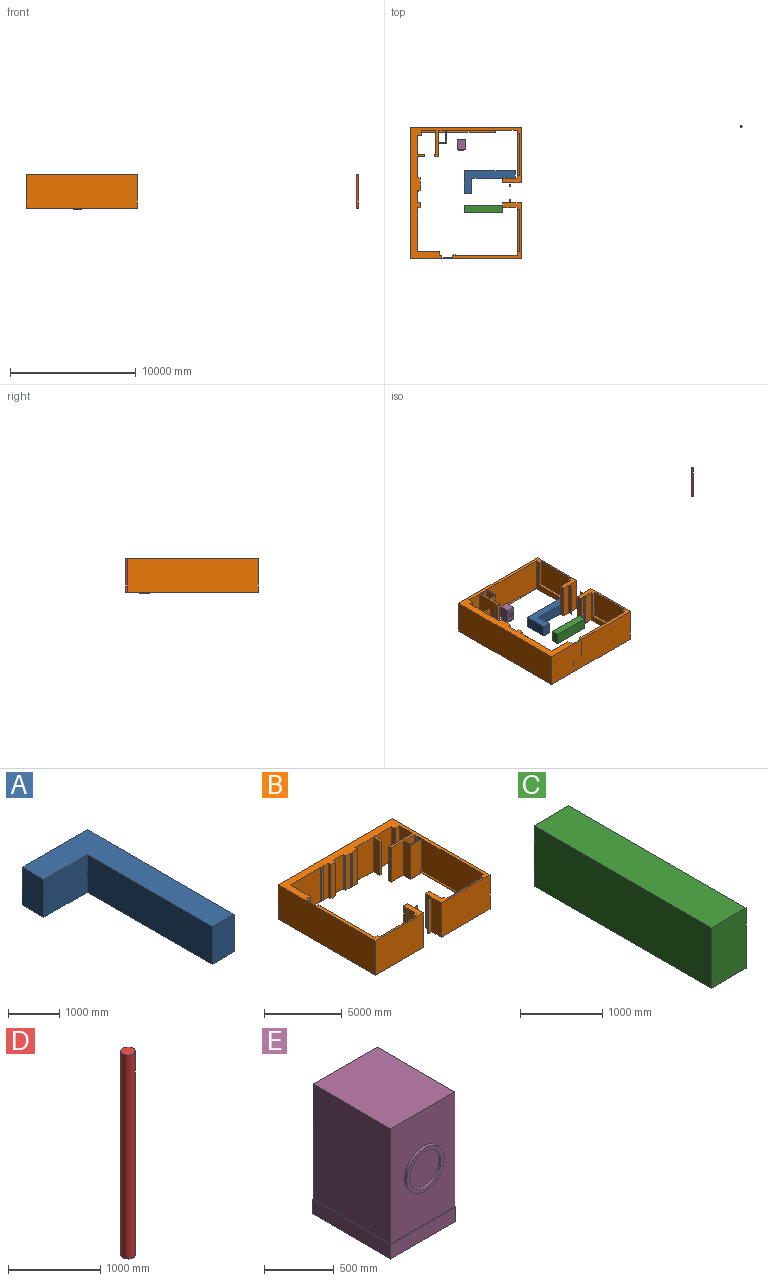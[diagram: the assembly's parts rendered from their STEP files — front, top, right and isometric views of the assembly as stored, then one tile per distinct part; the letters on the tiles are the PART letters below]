
ASSEMBLY  parts=5 mates=9
PART A: 8 faces, bbox 1800x4050x900 mm
  f0: plane 900x600mm, normal (-1,0,0), area 540000mm2, adj f1,f5,f6,f7
  f1: plane 1200x900mm, normal (0,-1,0), area 1080000mm2, adj f0,f2,f6,f7
  f2: plane 3450x900mm, normal (-1,0,0), area 3105000mm2, adj f1,f3,f6,f7
  f3: plane 900x600mm, normal (0,-1,0), area 540000mm2, adj f2,f4,f6,f7
  f4: plane 4050x900mm, normal (1,0,0), area 3645000mm2, adj f3,f5,f6,f7
  f5: plane 1800x900mm, normal (0,1,0), area 1620000mm2, adj f0,f4,f6,f7
  f6: plane 4050x1800mm, normal (0,0,-1), area 3150000mm2, adj f0,f1,f2,f3,f4,f5
  f7: plane 4050x1800mm, normal (0,0,1), area 3150000mm2, adj f0,f1,f2,f3,f4,f5
PART B: 107 faces, bbox 10433x8851.6x2700 mm
  f0: plane 2234.92x220mm, normal (-1,0,0), area 491681.4mm2, adj f40,f42,f94,f106
  f1: plane 2234.92x220mm, normal (-1,0,0), area 491681.4mm2, adj f6,f8,f94,f105
  f2: plane 2700x1080mm, normal (0,-1,0), area 2916000mm2, adj f3,f93,f94,f95
  f3: plane 2700x675mm, normal (-1,0,0), area 1822500mm2, adj f2,f4,f94,f95
  f4: plane 2700x1020mm, normal (0,-1,0), area 2744496.7mm2, adj f3,f5,f94,f95,f103
  f5: plane 5595x2700mm, normal (-1,0,0), area 15106500mm2, adj f4,f8,f94,f95
  f6: plane 3335x2234.92mm, normal (0,1,0), area 7453443.4mm2, adj f1,f7,f94,f105
  f7: plane 2234.92x220mm, normal (1,0,0), area 491681.4mm2, adj f6,f8,f94,f105
  f8: plane 3805x2700mm, normal (0,1,0), area 2820056.6mm2, adj f1,f5,f7,f9,f94,f95,f105
  f9: plane 2700x595mm, normal (1,0,0), area 1606500mm2, adj f8,f10,f94,f95
  f10: plane 2700x40mm, normal (0,-1,0), area 108000mm2, adj f9,f11,f94,f95
  f11: plane 2700x150mm, normal (1,0,0), area 405000mm2, adj f10,f12,f94,f95
  f12: plane 2700x40mm, normal (0,1,0), area 108000mm2, adj f11,f13,f94,f95
  f13: plane 2700x165.28mm, normal (1,0,0), area 446266.3mm2, adj f12,f14,f94,f95
  f14: plane 2700x40.98mm, normal (0,-1,0), area 110641.5mm2, adj f13,f15,f94,f95
  f15: plane 2700x143.9mm, normal (1,0,0), area 388534.6mm2, adj f14,f16,f94,f95
  f16: plane 2700x40.98mm, normal (0,1,0), area 110641.5mm2, adj f15,f17,f94,f95
  f17: plane 2700x75.81mm, normal (1,0,0), area 204699.1mm2, adj f16,f18,f94,f95
  f18: plane 2700x370mm, normal (0,1,0), area 999000mm2, adj f17,f19,f94,f95
  f19: plane 2700x560mm, normal (-1,0,0), area 1512000mm2, adj f18,f20,f94,f95
  f20: plane 2700x310.51mm, normal (0,1,0), area 838376.4mm2, adj f19,f21,f94,f95
  f21: plane 2700x50mm, normal (-1,0,0), area 135000mm2, adj f20,f22,f94,f95
  f22: plane 2700x310.51mm, normal (0,-1,0), area 838376.4mm2, adj f21,f23,f94,f95
  f23: plane 2700x870mm, normal (-1,0,0), area 2349000mm2, adj f22,f24,f94,f95
  f24: plane 4429x2700mm, normal (0,-1,0), area 11958300mm2, adj f23,f25,f94,f95
  f25: plane 8851.56x2700mm, normal (1,0,0), area 23899202.3mm2, adj f24,f26,f94,f95
  f26: plane 10433x2700mm, normal (0,1,0), area 28169100mm2, adj f25,f27,f94,f95
  f27: plane 8851.56x2700mm, normal (-1,0,0), area 23899202.3mm2, adj f26,f28,f94,f95
  f28: plane 4424x2700mm, normal (0,-1,0), area 11944800mm2, adj f27,f29,f94,f95
  f29: plane 2700x870mm, normal (1,0,0), area 2349000mm2, adj f28,f30,f94,f95
  f30: plane 2700x264.49mm, normal (0,-1,0), area 714123.6mm2, adj f29,f31,f94,f95
  f31: plane 2700x50mm, normal (1,0,0), area 135000mm2, adj f30,f32,f94,f95
  f32: plane 2700x264.49mm, normal (0,1,0), area 714123.6mm2, adj f31,f33,f94,f95
  f33: plane 2700x560mm, normal (1,0,0), area 1512000mm2, adj f32,f34,f94,f95
  f34: plane 2700x370mm, normal (0,1,0), area 999000mm2, adj f33,f35,f94,f95
  f35: plane 2700x325mm, normal (-1,0,0), area 877500mm2, adj f34,f36,f94,f95
  f36: plane 2700x40mm, normal (0,1,0), area 108000mm2, adj f35,f37,f94,f95
  f37: plane 2700x150mm, normal (-1,0,0), area 405000mm2, adj f36,f38,f94,f95
  f38: plane 2700x40mm, normal (0,-1,0), area 108000mm2, adj f37,f39,f94,f95
  f39: plane 2700x655mm, normal (-1,0,0), area 1768500mm2, adj f38,f42,f94,f95
  f40: plane 3350x2234.92mm, normal (0,1,0), area 7486967.1mm2, adj f0,f41,f94,f106
  f41: plane 2234.92x220mm, normal (1,0,0), area 491681.4mm2, adj f40,f42,f94,f106
  f42: plane 3800x2700mm, normal (0,1,0), area 2773032.9mm2, adj f0,f39,f41,f43,f94,f95,f106
  f43: plane 4916.91x2700mm, normal (1,0,0), area 13275652.3mm2, adj f42,f44,f94,f95
  f44: plane 2700x40mm, normal (0,-1,0), area 108000mm2, adj f43,f45,f94,f95
  f45: plane 2700x150mm, normal (1,0,0), area 405000mm2, adj f44,f46,f94,f95
  f46: plane 2700x40mm, normal (0,1,0), area 108000mm2, adj f45,f47,f94,f95
  f47: plane 2700x23.09mm, normal (1,0,0), area 62347.7mm2, adj f46,f48,f94,f95
  f48: plane 2700x200mm, normal (0,1,0), area 540000mm2, adj f47,f49,f94,f95
  f49: plane 2700x870mm, normal (1,0,0), area 2349000mm2, adj f48,f50,f94,f95
  f50: plane 2700x200mm, normal (0,-1,0), area 540000mm2, adj f49,f51,f94,f95
  f51: plane 2700x170mm, normal (1,0,0), area 459000mm2, adj f50,f52,f94,f95
  f52: plane 2700x300mm, normal (0,-1,0), area 810000mm2, adj f51,f53,f94,f95
  f53: plane 2700x1800mm, normal (1,0,0), area 4860000mm2, adj f52,f54,f94,f95
  f54: plane 2785x2700mm, normal (0,-1,0), area 7519500mm2, adj f53,f55,f94,f95
  f55: plane 2700x40mm, normal (-1,0,0), area 108000mm2, adj f54,f56,f94,f95
  f56: plane 2700x150mm, normal (0,-1,0), area 405000mm2, adj f55,f57,f94,f95
  f57: plane 2700x40mm, normal (1,0,0), area 108000mm2, adj f56,f58,f94,f95
  f58: plane 2700x525mm, normal (0,-1,0), area 1417500mm2, adj f57,f59,f94,f95
  f59: plane 2700x230mm, normal (-1,0,0), area 621000mm2, adj f58,f60,f94,f95
  f60: plane 2700x445mm, normal (0,-1,0), area 1201500mm2, adj f59,f61,f94,f95
  f61: plane 2700x230mm, normal (1,0,0), area 621000mm2, adj f60,f62,f94,f95
  f62: plane 2700x900mm, normal (0,-1,0), area 2430000mm2, adj f61,f63,f94,f95
  f63: plane 2700x70.97mm, normal (-1,0,0), area 191611.9mm2, adj f62,f64,f94,f95
  f64: plane 2700x32.69mm, normal (0,1,0), area 88264.4mm2, adj f63,f65,f94,f95
  f65: plane 2700x66.16mm, normal (-1,0,0), area 178631.3mm2, adj f64,f66,f94,f95
  f66: plane 2700x32.69mm, normal (0,-1,0), area 88264.4mm2, adj f65,f67,f94,f95
  f67: plane 2700x92.87mm, normal (-1,0,0), area 250756.8mm2, adj f66,f68,f94,f95
  f68: plane 2700x445mm, normal (0,-1,0), area 1201500mm2, adj f67,f69,f94,f95
  f69: plane 2700x40mm, normal (-1,0,0), area 108000mm2, adj f68,f70,f94,f95
  f70: plane 2700x150mm, normal (0,-1,0), area 405000mm2, adj f69,f71,f94,f95
  f71: plane 2700x40mm, normal (1,0,0), area 108000mm2, adj f70,f72,f94,f95
  f72: plane 2700x465mm, normal (0,-1,0), area 1255500mm2, adj f71,f73,f94,f95
  f73: plane 2700x230mm, normal (1,0,0), area 621000mm2, adj f72,f74,f94,f95
  f74: plane 2700x1660mm, normal (0,-1,0), area 4469250mm2, adj f73,f75,f94,f95,f96,f97,f98,f99
  f75: plane 2700x610mm, normal (-1,0,0), area 1647000mm2, adj f74,f76,f94,f95
  f76: plane 2700x160mm, normal (0,-1,0), area 432000mm2, adj f75,f77,f94,f95
  f77: plane 2700x610mm, normal (1,0,0), area 1647000mm2, adj f76,f78,f94,f95
  f78: plane 2700x1530mm, normal (0,-1,0), area 4131000mm2, adj f77,f79,f94,f95
  f79: plane 2700x320mm, normal (-1,0,0), area 864000mm2, adj f78,f80,f94,f95
  f80: plane 2700x410mm, normal (0,-1,0), area 1097496.7mm2, adj f79,f81,f94,f95,f102
  f81: plane 2700x1155mm, normal (-1,0,0), area 3118500mm2, adj f80,f82,f94,f95
  f82: plane 2700x1940mm, normal (0,1,0), area 5228496.7mm2, adj f81,f83,f94,f95,f102
  f83: plane 2700x65mm, normal (1,0,0), area 175500mm2, adj f82,f84,f94,f95
  f84: plane 2700x160mm, normal (0,1,0), area 432000mm2, adj f83,f93,f94,f95
  f85: plane 2700x625mm, normal (1,0,0), area 1687500mm2, adj f86,f92,f94,f95
  f86: plane 2700x970mm, normal (0,-1,0), area 2609496.7mm2, adj f85,f87,f94,f95,f101
  f87: plane 2700x100mm, normal (-1,0,0), area 270000mm2, adj f86,f88,f94,f95
  f88: plane 2700x40mm, normal (0,1,0), area 108000mm2, adj f87,f89,f94,f95
  f89: plane 2700x150mm, normal (-1,0,0), area 405000mm2, adj f88,f90,f94,f95
  f90: plane 2700x40mm, normal (0,-1,0), area 108000mm2, adj f89,f91,f94,f95
  f91: plane 2700x375mm, normal (-1,0,0), area 1012500mm2, adj f90,f92,f94,f95
  f92: plane 2700x970mm, normal (0,1,0), area 2609496.7mm2, adj f85,f91,f94,f95,f101
  f93: plane 2700x250mm, normal (-1,0,0), area 675000mm2, adj f2,f84,f94,f95
  f94: plane 10433x8851.56mm, normal (0,0,1), area 13950447.5mm2, adj f0,f1,f2,f3,f4,f5,f6,f7
  f95: plane 10433x8851.56mm, normal (0,0,-1), area 15421147.5mm2, adj f2,f3,f4,f5,f8,f9,f10,f11
  f96: plane 150x40mm, normal (0,0,1), area 6000mm2, adj f74,f97,f99,f100
  f97: plane 85x40mm, normal (-1,0,0), area 3400mm2, adj f74,f96,f98,f100
  f98: plane 150x40mm, normal (0,0,-1), area 6000mm2, adj f74,f97,f99,f100
  f99: plane 85x40mm, normal (1,0,0), area 3400mm2, adj f74,f96,f98,f100
  f100: plane 150x85mm, normal (0,-1,0), area 12750mm2, adj f96,f97,f98,f99
  f101: cylinder r=55mm len=625mm, axis (0,1,0), area 215984.5mm2, adj f86,f92
  f102: cylinder r=55mm len=1155mm, axis (0,1,0), area 399139.3mm2, adj f80,f82
  f103: cylinder r=55mm len=3885mm, axis (0,1,0), area 1342559.6mm2, adj f4,f104
  f104: plane 110x110mm, normal (0,-1,0), area 9503.3mm2, adj f103
  f105: plane 3335x220mm, normal (0,0,1), area 733700mm2, adj f1,f6,f7,f8
  f106: plane 3350x220mm, normal (0,0,1), area 737000mm2, adj f0,f40,f41,f42
PART C: 6 faces, bbox 600x3050x900 mm
  f0: plane 900x600mm, normal (0,-1,0), area 540000mm2, adj f1,f3,f4,f5
  f1: plane 3050x900mm, normal (1,0,0), area 2745000mm2, adj f0,f2,f4,f5
  f2: plane 900x600mm, normal (0,1,0), area 540000mm2, adj f1,f3,f4,f5
  f3: plane 3050x900mm, normal (-1,0,0), area 2745000mm2, adj f0,f2,f4,f5
  f4: plane 3050x600mm, normal (0,0,-1), area 1830000mm2, adj f0,f1,f2,f3
  f5: plane 3050x600mm, normal (0,0,1), area 1830000mm2, adj f0,f1,f2,f3
PART D: 3 faces, bbox 154.2x154.2x2700 mm
  f0: cylinder r=77.11mm len=2700mm, axis (0,0,-1), area 1308094.7mm2, adj f1,f2
  f1: plane 154.21x154.21mm, normal (0,0,1), area 18678.5mm2, adj f0
  f2: plane 154.21x154.21mm, normal (0,0,-1), area 18678.5mm2, adj f0
PART E: 15 faces, bbox 660x820x1138 mm
  f0: plane 800x660mm, normal (0,0,1), area 14500mm2, adj f1,f2,f3,f4,f6,f7,f8,f9
  f1: plane 800x127mm, normal (-1,0,0), area 101600mm2, adj f0,f2,f4,f5
  f2: plane 660x127mm, normal (0,-1,0), area 83820mm2, adj f0,f1,f3,f5
  f3: plane 800x127mm, normal (1,0,0), area 101600mm2, adj f0,f2,f4,f5
  f4: plane 660x127mm, normal (0,1,0), area 83820mm2, adj f0,f1,f3,f5
  f5: plane 800x660mm, normal (0,0,-1), area 528000mm2, adj f1,f2,f3,f4
  f6: plane 1011x650mm, normal (0,1,0), area 657150mm2, adj f0,f7,f9,f10
  f7: plane 1011x790mm, normal (-1,0,0), area 798690mm2, adj f0,f6,f8,f10
  f8: plane 1011x650mm, normal (0,-1,0), area 543738.5mm2, adj f0,f7,f9,f10,f11
  f9: plane 1011x790mm, normal (1,0,0), area 798690mm2, adj f0,f6,f8,f10
  f10: plane 790x650mm, normal (0,0,1), area 513500mm2, adj f6,f7,f8,f9
  f11: cylinder r=190mm len=380mm, axis (0,1,0), area 29845.1mm2, adj f8,f12
  f12: plane 380x380mm, normal (0,-1,0), area 34554.7mm2, adj f11,f13
  f13: cylinder r=158.43mm len=316.87mm, axis (0,-1,0), area 19909.2mm2, adj f12,f14
  f14: plane 316.87x316.87mm, normal (0,-1,0), area 78856.8mm2, adj f13
PLACE A rot(axis=(0,0,1),90deg) t=(-1999.77,706.37,3992.34)mm
PLACE B rot(axis=(0,0,1),90deg) t=(-869.77,-3453.63,3092.34)mm
PLACE C rot(axis=(0,0,1),90deg) t=(-1999.77,516.6,3992.34)mm
PLACE D rot(axis=(-1,0,0),0deg) t=(6603.15,5007.48,3092.34)mm
PLACE E rot(axis=(-1,0,0),0deg) t=(-5635.72,4922.95,2965.34)mm
MATE parallel B.f24 <-> E.f9  axis (1,0,0) through (-519.77,4510.87,4442.34)mm
MATE planar C.f0 <-> B.f34  axis (1,0,0) through (-1999.77,216.6,3542.34)mm
MATE planar A.f6 <-> B.f95  axis (0,0,-1) through (-3419.05,2760.66,3092.34)mm
MATE planar C.f0 <-> B.f34  axis (1,0,0) through (-1999.77,216.6,3542.34)mm
MATE planar B.f9 <-> A.f2  axis (0,1,0) through (-1167.27,2666.37,4442.34)mm
MATE planar C.f2 <-> A.f5  axis (-1,0,0) through (-5049.77,516.6,3992.34)mm
MATE planar B.f95 <-> C.f4  axis (0,0,-1) through (-8799.77,4531.37,3092.34)mm
MATE planar B.f94 <-> D.f0  axis (0,0,1) through (-6287.4,1593.36,5792.34)mm
MATE planar B.f95 <-> E.f0  axis (0,0,-1) through (-519.77,6725.37,3092.34)mm
